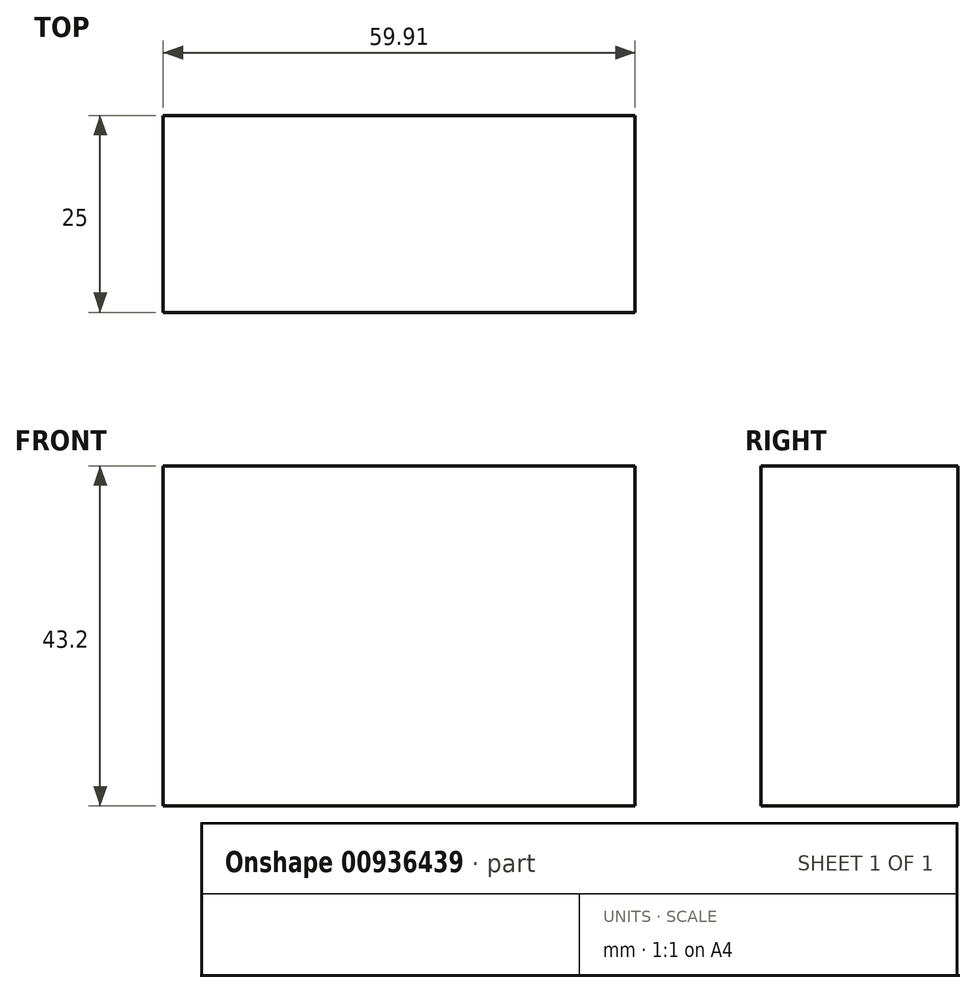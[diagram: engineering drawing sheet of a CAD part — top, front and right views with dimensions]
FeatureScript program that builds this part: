
annotation { "Feature Type Name" : "Feature", "Feature Type Description" : "" }
export const myFeature = defineFeature(function(context is Context, id is Id, definition is map)
    precondition{}
    {
        {
            var Q0;
            Q0=qCreatedBy(makeId("Front.planeOp"),FACE);
            var sketch = newSketch(context, id + "F0", { "sketchPlane" : qUnion([Q0])});
            skLineSegment(sketch, "E0.bottom", {"start": v(-88.1, 21.47) * mm, "end": v(-28.2, 21.47) * mm});
            skLineSegment(sketch, "E0.top", {"start": v(-88.1, -21.73) * mm, "end": v(-28.2, -21.73) * mm});
            skLineSegment(sketch, "E0.left", {"start": v(-88.1, 21.47) * mm, "end": v(-88.1, -21.73) * mm});
            skLineSegment(sketch, "E0.right", {"start": v(-28.2, 21.47) * mm, "end": v(-28.2, -21.73) * mm});
            skSolve(sketch);
        }
        {
            var Q0;
            Q0 = qSketchRegion(id + "F0", true);
            extrude(context, id + "F1", {"entities" : qUnion([Q0]), "depth" : 25 * mm, "offsetDistance" : 25 * mm});
        }
    });
